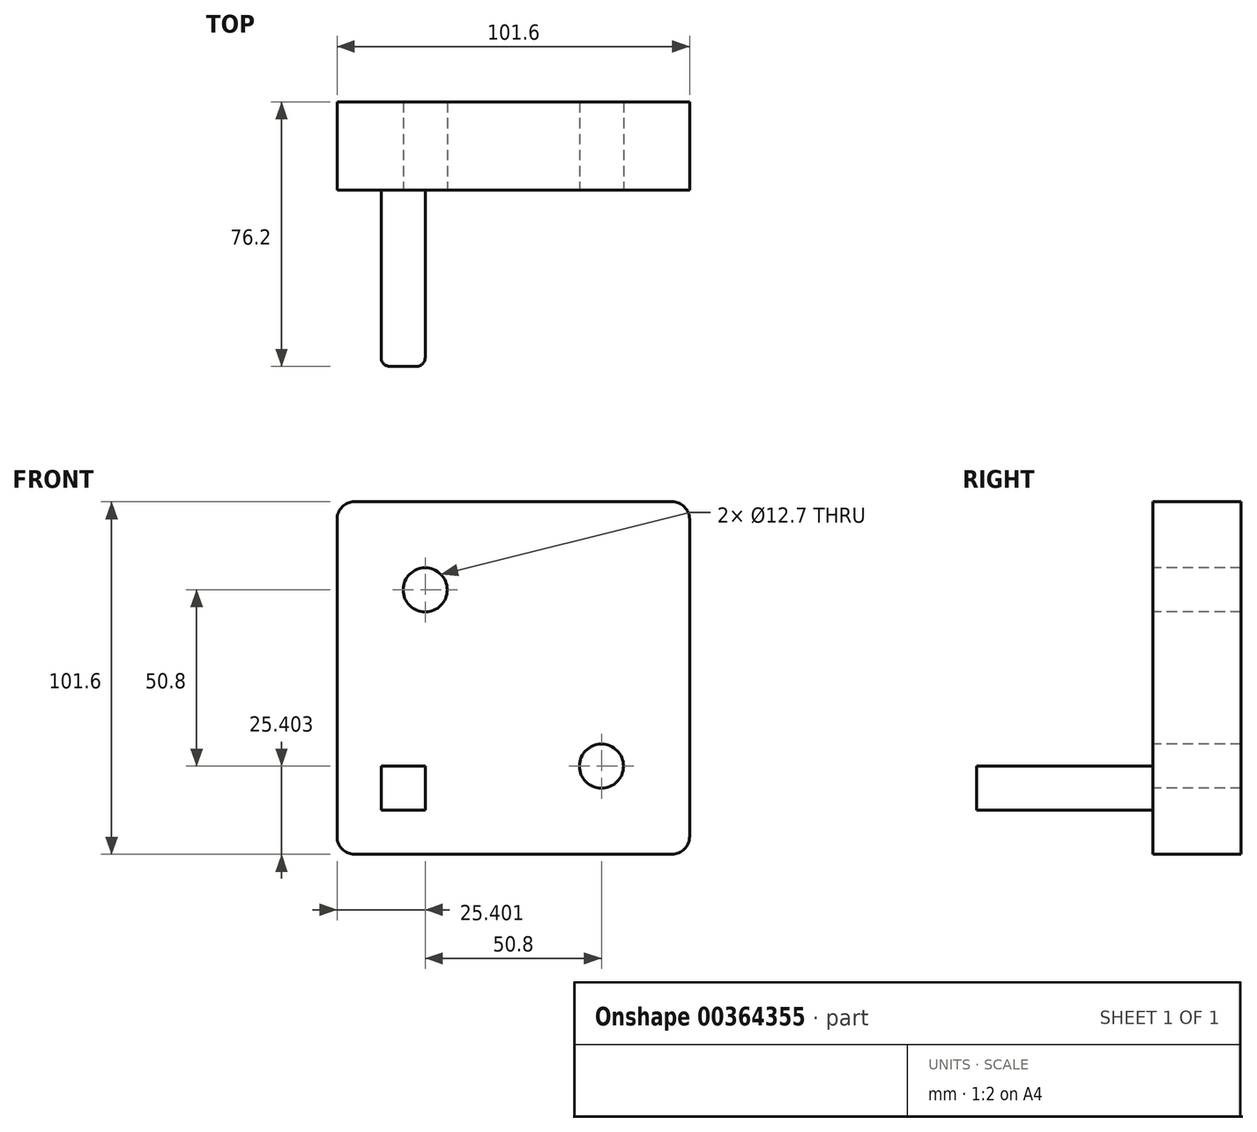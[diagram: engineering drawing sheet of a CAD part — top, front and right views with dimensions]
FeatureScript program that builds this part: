
annotation { "Feature Type Name" : "Feature", "Feature Type Description" : "" }
export const myFeature = defineFeature(function(context is Context, id is Id, definition is map)
    precondition{}
    {
        {
            var Q0;
            Q0=qCreatedBy(makeId("Front.planeOp"),FACE);
            var sketch = newSketch(context, id + "F0", { "sketchPlane" : qUnion([Q0])});
            skLineSegment(sketch, "E0.bottom", {"start": v(-59.72, 61.21) * mm, "end": v(41.88, 61.21) * mm});
            skLineSegment(sketch, "E0.top", {"start": v(-59.72, -40.39) * mm, "end": v(41.88, -40.39) * mm});
            skLineSegment(sketch, "E0.left", {"start": v(-59.72, 61.21) * mm, "end": v(-59.72, -40.39) * mm});
            skLineSegment(sketch, "E0.right", {"start": v(41.88, 61.21) * mm, "end": v(41.88, -40.39) * mm});
            skSolve(sketch);
        }
        {
            var Q0;
            Q0=makeQuery(id+"F0.imprint","IMPRINT",FACE,{"disambiguationData":[TD([[makeQuery(id+"F0.imprint","IMPRINT",EDGE,{"derivedFrom":sQuery(id+"F0.wireOp",EDGE,"E0.bottom")}),-1.0]])]});
            extrude(context, id + "F1", {"entities" : qUnion([Q0]), "depth" : 25.4 * mm});
        }
        {
            var Q0;
            Q0=makeQuery(id+"F1.opExtrude","SWEPT_EDGE",EDGE,{"disambiguationData":[OSD([sQuery(id+"F0.wireOp",EDGE,"E0.bottom"),sQuery(id+"F0.wireOp",EDGE,"E0.left")])]});
            fillet(context, id + "F2", {"entities" : qUnion([Q0]), "radius" : 5.08 * mm, "tangentPropagation" : true, "allowEdgeOverflow" : false});
        }
        {
            var Q0;
            Q0=makeQuery(id+"F1.opExtrude","SWEPT_EDGE",EDGE,{"disambiguationData":[OSD([sQuery(id+"F0.wireOp",EDGE,"E0.top"),sQuery(id+"F0.wireOp",EDGE,"E0.left")])]});
            fillet(context, id + "F3", {"entities" : qUnion([Q0]), "radius" : 5.08 * mm, "tangentPropagation" : true, "allowEdgeOverflow" : false});
        }
        {
            var Q0;
            Q0=makeQuery(id+"F1.opExtrude","SWEPT_EDGE",EDGE,{"disambiguationData":[OSD([sQuery(id+"F0.wireOp",EDGE,"E0.top"),sQuery(id+"F0.wireOp",EDGE,"E0.right")])]});
            fillet(context, id + "F4", {"entities" : qUnion([Q0]), "radius" : 5.08 * mm, "tangentPropagation" : true, "allowEdgeOverflow" : false});
        }
        {
            var Q0;
            Q0=makeQuery(id+"F1.opExtrude","SWEPT_EDGE",EDGE,{"disambiguationData":[OSD([sQuery(id+"F0.wireOp",EDGE,"E0.bottom"),sQuery(id+"F0.wireOp",EDGE,"E0.right")])]});
            fillet(context, id + "F5", {"entities" : qUnion([Q0]), "radius" : 5.08 * mm, "tangentPropagation" : true, "allowEdgeOverflow" : false});
        }
        {
            var Q0;
            Q0=makeQuery(id+"F1.opExtrude","CAP_FACE",FACE,{"disambiguationData":[OSD([sQuery(id+"F0.wireOp",EDGE,"E0.bottom"),sQuery(id+"F0.wireOp",EDGE,"E0.top"),sQuery(id+"F0.wireOp",EDGE,"E0.left"),sQuery(id+"F0.wireOp",EDGE,"E0.right")])],"isStart":false});
            var sketch = newSketch(context, id + "F6", { "sketchPlane" : qUnion([Q0])});
            skPoint(sketch, "E1", {"position": v(-34.32, 35.81) * mm});
            skSolve(sketch);
        }
        {
            var Q0;
            {var subQ1=sQuery(id+"F0.wireOp",EDGE,"E0.left");Q0=makeQuery(id+"F6.imprint","IMPRINT",FACE,{"disambiguationData":[TD([[makeQuery(id+"F6.imprint","IMPRINT",EDGE,{"derivedFrom":makeQuery(id+"F1.opExtrude","CAP_EDGE",EDGE,{"disambiguationData":[OSD([subQ1])],"isStart":false})}),1.0]])]});}
            var sketch = newSketch(context, id + "F7", { "sketchPlane" : qUnion([Q0])});
            skPoint(sketch, "E2", {"position": v(16.48, -14.99) * mm});
            skSolve(sketch);
        }
        {
            var Q0;
            Q0=sQuery(id+"F6.wireOp",VERTEX,"E1");
            var Q1;
            Q1=sQuery(id+"F7.wireOp",VERTEX,"E2");
            var Q2;
            Q2=makeQuery(id+"F1.opExtrude","SWEPT_BODY",BODY,{"disambiguationData":[OSD([sQuery(id+"F0.wireOp",EDGE,"E0.bottom"),sQuery(id+"F0.wireOp",EDGE,"E0.top"),sQuery(id+"F0.wireOp",EDGE,"E0.left"),sQuery(id+"F0.wireOp",EDGE,"E0.right")])]});
            hole(context, id + "F8", {"style" : HoleStyle.SIMPLE, "endStyle" : HoleEndStyle.THROUGH, "holeDiameter" : 12.7 * mm, "isTappedThrough" : true, "tappedDepth" : 12.7 * mm, "tapClearance" : 3, "locations" : qUnion([Q0, Q1]), "scope" : qUnion([Q2])});
        }
        {
            var Q0;
            Q0=makeQuery(id+"F1.opExtrude","CAP_FACE",FACE,{"disambiguationData":[OSD([sQuery(id+"F0.wireOp",EDGE,"E0.bottom"),sQuery(id+"F0.wireOp",EDGE,"E0.top"),sQuery(id+"F0.wireOp",EDGE,"E0.left"),sQuery(id+"F0.wireOp",EDGE,"E0.right")])],"isStart":false});
            var sketch = newSketch(context, id + "F9", { "sketchPlane" : qUnion([Q0])});
            skSolve(sketch);
        }
        {
            var Q0;
            {var subQ1=sQuery(id+"F0.wireOp",EDGE,"E0.left");Q0=makeQuery(id+"F9.imprint","IMPRINT",FACE,{"disambiguationData":[TD([[makeQuery(id+"F9.imprint","IMPRINT",EDGE,{"derivedFrom":makeQuery(id+"F1.opExtrude","CAP_EDGE",EDGE,{"disambiguationData":[OSD([subQ1])],"isStart":false})}),1.0]])]});}
            var sketch = newSketch(context, id + "F10", { "sketchPlane" : qUnion([Q0])});
            skLineSegment(sketch, "E3.bottom", {"start": v(-47.02, -14.99) * mm, "end": v(-34.32, -14.99) * mm});
            skLineSegment(sketch, "E3.top", {"start": v(-47.02, -27.69) * mm, "end": v(-34.32, -27.69) * mm});
            skLineSegment(sketch, "E3.left", {"start": v(-47.02, -14.99) * mm, "end": v(-47.02, -27.69) * mm});
            skLineSegment(sketch, "E3.right", {"start": v(-34.32, -14.99) * mm, "end": v(-34.32, -27.69) * mm});
            skSolve(sketch);
        }
        {
            var Q0;
            Q0=makeQuery(id+"F10.imprint","IMPRINT",FACE,{"disambiguationData":[TD([[makeQuery(id+"F10.imprint","IMPRINT",EDGE,{"derivedFrom":sQuery(id+"F10.wireOp",EDGE,"E3.bottom")}),-1.0]])]});
            extrude(context, id + "F11", {"entities" : qUnion([Q0]), "operationType" : NewBodyOperationType.ADD, "depth" : 50.8 * mm});
        }
        {
            var Q0;
            Q0=makeQuery(id+"F11.opExtrude","CAP_EDGE",EDGE,{"disambiguationData":[OSD([sQuery(id+"F10.wireOp",EDGE,"E3.right")])],"isStart":false});
            fillet(context, id + "F12", {"entities" : qUnion([Q0]), "radius" : 2.54 * mm, "tangentPropagation" : true, "allowEdgeOverflow" : false});
        }
        {
            var Q0;
            Q0=makeQuery(id+"F11.opExtrude","CAP_EDGE",EDGE,{"disambiguationData":[OSD([sQuery(id+"F10.wireOp",EDGE,"E3.left")])],"isStart":false});
            fillet(context, id + "F13", {"entities" : qUnion([Q0]), "radius" : 2.54 * mm, "tangentPropagation" : true, "allowEdgeOverflow" : false});
        }
    });
